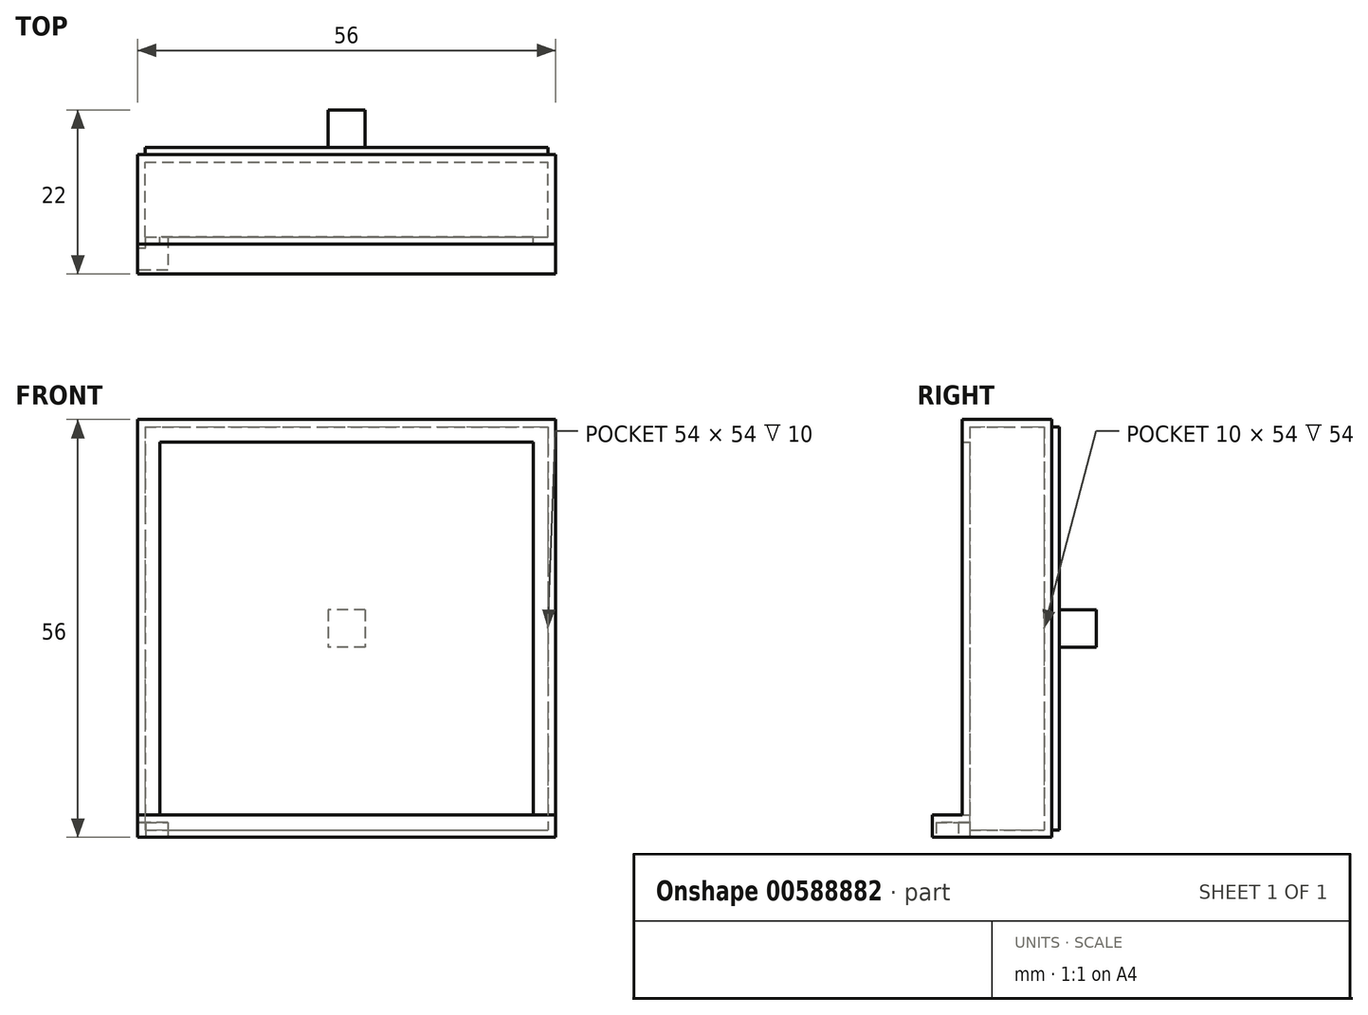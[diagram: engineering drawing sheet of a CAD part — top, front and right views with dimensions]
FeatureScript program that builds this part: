
annotation { "Feature Type Name" : "Feature", "Feature Type Description" : "" }
export const myFeature = defineFeature(function(context is Context, id is Id, definition is map)
    precondition{}
    {
        {
            var Q0;
            Q0=qCreatedBy(makeId("Front.planeOp"),FACE);
            var sketch = newSketch(context, id + "F0", { "sketchPlane" : qUnion([Q0])});
            skLineSegment(sketch, "E0.bottom", {"start": v(-27, 27) * mm, "end": v(27, 27) * mm});
            skLineSegment(sketch, "E0.top", {"start": v(-27, -27) * mm, "end": v(27, -27) * mm});
            skLineSegment(sketch, "E0.left", {"start": v(-27, 27) * mm, "end": v(-27, -27) * mm});
            skLineSegment(sketch, "E0.right", {"start": v(27, 27) * mm, "end": v(27, -27) * mm});
            skPoint(sketch, "E0.middle", {"position": v(0, 0) * mm});
            skLineSegment(sketch, "E1.0", {"start": v(-28, 28) * mm, "end": v(28, 28) * mm});
            skLineSegment(sketch, "E1.1", {"start": v(-28, 28) * mm, "end": v(-28, -28) * mm});
            skLineSegment(sketch, "E1.2", {"start": v(-28, -28) * mm, "end": v(28, -28) * mm});
            skLineSegment(sketch, "E1.3", {"start": v(28, 28) * mm, "end": v(28, -28) * mm});
            skSolve(sketch);
        }
        {
            var Q0;
            Q0 = qSketchRegion(id + "F0", true);
            extrude(context, id + "F1", {"entities" : qUnion([Q0]), "depth" : 10 * mm, "offsetDistance" : 25 * mm});
        }
        {
            var Q0;
            Q0=makeQuery(id+"F1.opExtrude","CAP_FACE",FACE,{"disambiguationData":[OSD([sQuery(id+"F0.wireOp",EDGE,"E0.bottom"),sQuery(id+"F0.wireOp",EDGE,"E0.top"),sQuery(id+"F0.wireOp",EDGE,"E0.left"),sQuery(id+"F0.wireOp",EDGE,"E0.right"),sQuery(id+"F0.wireOp",EDGE,"E1.0"),sQuery(id+"F0.wireOp",EDGE,"E1.1"),sQuery(id+"F0.wireOp",EDGE,"E1.2"),sQuery(id+"F0.wireOp",EDGE,"E1.3")])],"isStart":false});
            var sketch = newSketch(context, id + "F2", { "sketchPlane" : qUnion([Q0])});
            skLineSegment(sketch, "E2.0.0", {"start": v(-27, 27) * mm, "end": v(-27, -27) * mm});
            skLineSegment(sketch, "E2.0.1", {"start": v(-27, -27) * mm, "end": v(27, -27) * mm});
            skLineSegment(sketch, "E2.0.2", {"start": v(27, -27) * mm, "end": v(27, 27) * mm});
            skLineSegment(sketch, "E2.0.3", {"start": v(27, 27) * mm, "end": v(-27, 27) * mm});
            skLineSegment(sketch, "E3.0", {"start": v(-25, 25) * mm, "end": v(-25, -25) * mm});
            skLineSegment(sketch, "E3.1", {"start": v(25, 25) * mm, "end": v(-25, 25) * mm});
            skLineSegment(sketch, "E3.2", {"start": v(25, -25) * mm, "end": v(25, 25) * mm});
            skLineSegment(sketch, "E3.3", {"start": v(-25, -25) * mm, "end": v(25, -25) * mm});
            skSolve(sketch);
        }
        {
            var Q0;
            Q0=makeQuery(id+"F2.imprint","IMPRINT",FACE,{"disambiguationData":[TD([[makeQuery(id+"F2.imprint","IMPRINT",EDGE,{"derivedFrom":sQuery(id+"F2.wireOp",EDGE,"E2.0.0")}),-1.0]])]});
            var Q1;
            Q1=makeQuery(id+"F2.imprint","IMPRINT",FACE,{"disambiguationData":[TD([[makeQuery(id+"F2.imprint","IMPRINT",EDGE,{"derivedFrom":sQuery(id+"F2.wireOp",EDGE,"E2.0.0")}),1.0]])]});
            extrude(context, id + "F3", {"entities" : qUnion([Q0, Q1]), "operationType" : NewBodyOperationType.ADD, "depth" : 1 * mm, "offsetDistance" : 25 * mm});
        }
        {
            var Q0;
            Q0=makeQuery(id+"F0.imprint","IMPRINT",FACE,{"disambiguationData":[TD([[makeQuery(id+"F0.imprint","IMPRINT",EDGE,{"derivedFrom":sQuery(id+"F0.wireOp",EDGE,"E0.bottom")}),-1.0]])]});
            extrude(context, id + "F4", {"entities" : qUnion([Q0]), "oppositeDirection" : true, "depth" : 2 * mm, "offsetDistance" : 25 * mm});
        }
        {
            var Q0;
            Q0=makeQuery(id+"F4.opExtrude","CAP_FACE",FACE,{"disambiguationData":[OSD([sQuery(id+"F0.wireOp",EDGE,"E0.bottom"),sQuery(id+"F0.wireOp",EDGE,"E0.top"),sQuery(id+"F0.wireOp",EDGE,"E0.left"),sQuery(id+"F0.wireOp",EDGE,"E0.right")])],"isStart":false});
            var sketch = newSketch(context, id + "F5", { "sketchPlane" : qUnion([Q0])});
            skLineSegment(sketch, "E4.bottom", {"start": v(-2.5, 2.5) * mm, "end": v(2.5, 2.5) * mm});
            skLineSegment(sketch, "E4.top", {"start": v(-2.5, -2.5) * mm, "end": v(2.5, -2.5) * mm});
            skLineSegment(sketch, "E4.left", {"start": v(-2.5, 2.5) * mm, "end": v(-2.5, -2.5) * mm});
            skLineSegment(sketch, "E4.right", {"start": v(2.5, 2.5) * mm, "end": v(2.5, -2.5) * mm});
            skPoint(sketch, "E4.middle", {"position": v(0, 0) * mm});
            skSolve(sketch);
        }
        {
            var Q0;
            Q0 = qSketchRegion(id + "F5", true);
            extrude(context, id + "F6", {"entities" : qUnion([Q0]), "operationType" : NewBodyOperationType.ADD, "depth" : 5 * mm, "offsetDistance" : 25 * mm});
        }
        {
            var Q0;
            Q0=makeQuery(id+"F3.opExtrude","CAP_FACE",FACE,{"disambiguationData":[OSD([sQuery(id+"F0.wireOp",EDGE,"E1.0"),sQuery(id+"F0.wireOp",EDGE,"E1.1"),sQuery(id+"F0.wireOp",EDGE,"E1.2"),sQuery(id+"F0.wireOp",EDGE,"E1.3"),sQuery(id+"F2.wireOp",EDGE,"E3.0"),sQuery(id+"F2.wireOp",EDGE,"E3.1"),sQuery(id+"F2.wireOp",EDGE,"E3.2"),sQuery(id+"F2.wireOp",EDGE,"E3.3")])],"isStart":false});
            var sketch = newSketch(context, id + "F7", { "sketchPlane" : qUnion([Q0])});
            skLineSegment(sketch, "E5.0", {"start": v(-28, -28) * mm, "end": v(28, -28) * mm});
            skLineSegment(sketch, "E6.top", {"start": v(-28, -25) * mm, "end": v(28, -25) * mm});
            skLineSegment(sketch, "E6.left", {"start": v(-28, -28) * mm, "end": v(-28, -25) * mm});
            skLineSegment(sketch, "E6.right", {"start": v(28, -28) * mm, "end": v(28, -25) * mm});
            skSolve(sketch);
        }
        {
            var Q0;
            Q0=makeQuery(id+"F7.imprint","IMPRINT",FACE,{"disambiguationData":[TD([[makeQuery(id+"F7.imprint","IMPRINT",EDGE,{"derivedFrom":sQuery(id+"F7.wireOp",EDGE,"E5.0")}),1.0]])]});
            extrude(context, id + "F8", {"entities" : qUnion([Q0]), "operationType" : NewBodyOperationType.ADD, "depth" : 4 * mm, "offsetDistance" : 25 * mm});
        }
        {
            var Q0;
            {var subQ0=sQuery(id+"F0.wireOp",EDGE,"E1.2");Q0=makeQuery(id+"F8.boolean.opBoolean","MERGE",FACE,{"derivedFrom":[makeQuery(id+"F3.boolean.opBoolean","MERGE",FACE,{"derivedFrom":[makeQuery(id+"F1.opExtrude","SWEPT_FACE",FACE,{"disambiguationData":[OSD([subQ0])]}),makeQuery(id+"F3.opExtrude","SWEPT_FACE",FACE,{"disambiguationData":[OSD([subQ0])]})]}),makeQuery(id+"F8.opExtrude","SWEPT_FACE",FACE,{"disambiguationData":[OSD([sQuery(id+"F7.wireOp",EDGE,"E5.0")])]})]});}
            var sketch = newSketch(context, id + "F9", { "sketchPlane" : qUnion([Q0])});
            skLineSegment(sketch, "E7.0", {"start": v(-27, 10) * mm, "end": v(27, 10) * mm, "construction": true});
            skLineSegment(sketch, "E8", {"start": v(-23.95, 10) * mm, "end": v(-23.95, 14.5) * mm});
            skLineSegment(sketch, "E9", {"start": v(-23.95, 14.5) * mm, "end": v(-28, 14.5) * mm});
            skLineSegment(sketch, "E10", {"start": v(-28, 14.5) * mm, "end": v(-28, 11.5) * mm});
            skLineSegment(sketch, "E11", {"start": v(-28, 11.5) * mm, "end": v(-26.95, 11.5) * mm});
            skLineSegment(sketch, "E12", {"start": v(-26.95, 11.5) * mm, "end": v(-26.95, 10) * mm});
            skLineSegment(sketch, "E13", {"start": v(-26.95, 10) * mm, "end": v(-23.95, 10) * mm});
            skSolve(sketch);
        }
        {
            var Q0;
            Q0=makeQuery(id+"F9.imprint","IMPRINT",FACE,{"disambiguationData":[TD([[makeQuery(id+"F9.imprint","IMPRINT",EDGE,{"derivedFrom":sQuery(id+"F9.wireOp",EDGE,"E8")}),1.0]])]});
            extrude(context, id + "F10", {"entities" : qUnion([Q0]), "operationType" : NewBodyOperationType.REMOVE, "oppositeDirection" : true, "depth" : 2 * mm, "offsetDistance" : 25 * mm});
        }
        {
            var Q0;
            Q0=makeQuery(id+"F0.imprint","IMPRINT",FACE,{"disambiguationData":[TD([[makeQuery(id+"F0.imprint","IMPRINT",EDGE,{"derivedFrom":sQuery(id+"F0.wireOp",EDGE,"E0.bottom")}),1.0]])]});
            var Q1;
            Q1=makeQuery(id+"F0.imprint","IMPRINT",FACE,{"disambiguationData":[TD([[makeQuery(id+"F0.imprint","IMPRINT",EDGE,{"derivedFrom":sQuery(id+"F0.wireOp",EDGE,"E0.bottom")}),-1.0]])]});
            extrude(context, id + "F11", {"entities" : qUnion([Q0, Q1]), "operationType" : NewBodyOperationType.ADD, "oppositeDirection" : true, "depth" : 1 * mm, "offsetDistance" : 25 * mm});
        }
    });
